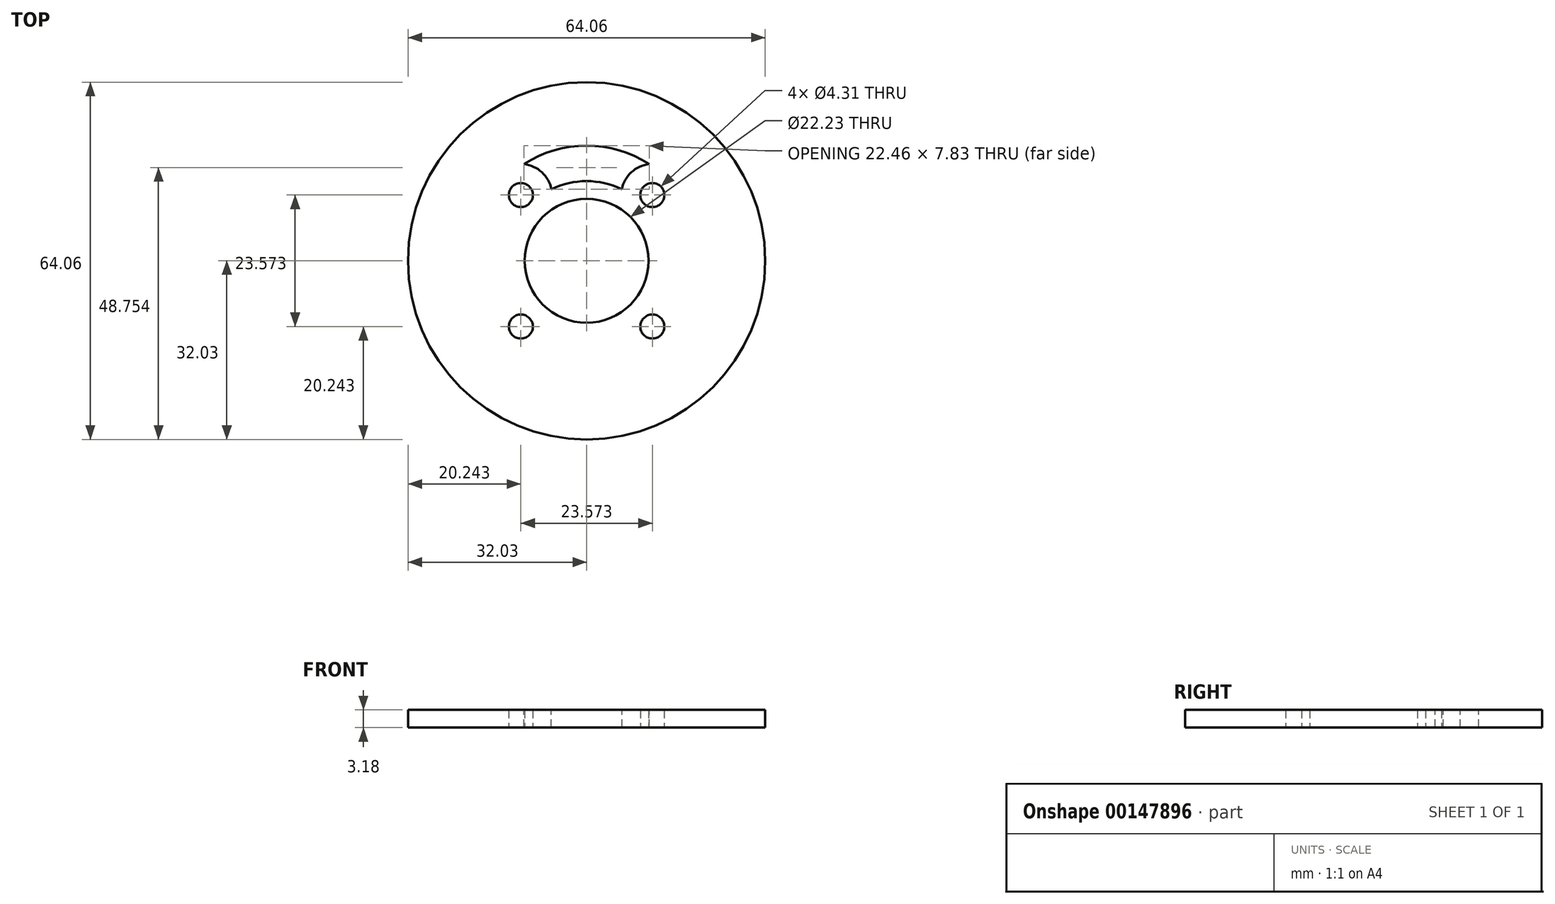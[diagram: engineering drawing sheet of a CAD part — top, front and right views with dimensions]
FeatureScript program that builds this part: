
annotation { "Feature Type Name" : "Feature", "Feature Type Description" : "" }
export const myFeature = defineFeature(function(context is Context, id is Id, definition is map)
    precondition{}
    {
        {
            var Q0;
            Q0=qCreatedBy(makeId("Top.planeOp"),FACE);
            var sketch = newSketch(context, id + "F0", { "sketchPlane" : qUnion([Q0])});
            skCircle(sketch, "E0", {"center": v(0, 0) * mm, "radius": 32.03 * mm});
            skCircle(sketch, "E1", {"center": v(0, 0) * mm, "radius": 11.11 * mm, "construction": true});
            skLineSegment(sketch, "E2.bottom", {"start": v(-11.79, -11.79) * mm, "end": v(11.79, -11.79) * mm, "construction": true});
            skLineSegment(sketch, "E2.top", {"start": v(-11.79, 11.79) * mm, "end": v(11.79, 11.79) * mm, "construction": true});
            skLineSegment(sketch, "E2.left", {"start": v(-11.79, -11.79) * mm, "end": v(-11.79, 11.79) * mm, "construction": true});
            skLineSegment(sketch, "E2.right", {"start": v(11.79, -11.79) * mm, "end": v(11.79, 11.79) * mm, "construction": true});
            skCircle(sketch, "E3", {"center": v(-11.79, -11.79) * mm, "radius": 5.56 * mm, "construction": true});
            skCircle(sketch, "E4", {"center": v(-11.79, -11.79) * mm, "radius": 2.15 * mm});
            skCircle(sketch, "E5", {"center": v(11.79, 11.79) * mm, "radius": 2.15 * mm});
            skCircle(sketch, "E6", {"center": v(11.79, -11.79) * mm, "radius": 2.15 * mm});
            skCircle(sketch, "E7", {"center": v(-11.79, 11.79) * mm, "radius": 2.15 * mm});
            skCircle(sketch, "E8", {"center": v(0, 0) * mm, "radius": 11.11 * mm});
            skSolve(sketch);
        }
        {
            var Q0;
            Q0=makeQuery(id+"F0.imprint","IMPRINT",FACE,{"disambiguationData":[TD([[makeQuery(id+"F0.imprint","IMPRINT",EDGE,{"derivedFrom":sQuery(id+"F0.wireOp",EDGE,"d7zeTPih-CRss-xDOh-gPdP-rmPCdwzH7cdN.left")}),1.0]])]});
            var Q1;
            Q1=makeQuery(id+"F0.imprint","IMPRINT",FACE,{"disambiguationData":[TD([[makeQuery(id+"F0.imprint","IMPRINT",EDGE,{"derivedFrom":sQuery(id+"F0.wireOp",EDGE,"E0")}),1.0]])]});
            extrude(context, id + "F1", {"entities" : qUnion([Q0, Q1]), "depth" : 3.17 * mm});
        }
        {
            var Q0;
            Q0=makeQuery(id+"F1.opExtrude","CAP_FACE",FACE,{"disambiguationData":[OSD([sQuery(id+"F0.wireOp",EDGE,"E0"),sQuery(id+"F0.wireOp",EDGE,"E4"),sQuery(id+"F0.wireOp",EDGE,"E5"),sQuery(id+"F0.wireOp",EDGE,"E6"),sQuery(id+"F0.wireOp",EDGE,"E7"),sQuery(id+"F0.wireOp",EDGE,"E8")])],"isStart":false});
            var sketch = newSketch(context, id + "F2", { "sketchPlane" : qUnion([Q0])});
            skArc(sketch, "E9", {"start": v(-6.33, 12.81) * mm, "mid": v(-8.03, 15.88) * mm, "end": v(-11.23, 17.31) * mm});
            skArc(sketch, "E10", {"start": v(11.23, 17.31) * mm, "mid": v(8.03, 15.88) * mm, "end": v(6.33, 12.81) * mm});
            skArc(sketch, "E11", {"start": v(11.23, 17.31) * mm, "mid": v(0, 20.64) * mm, "end": v(-11.23, 17.31) * mm});
            skArc(sketch, "E12", {"start": v(6.33, 12.81) * mm, "mid": v(0, 14.29) * mm, "end": v(-6.33, 12.81) * mm});
            skSolve(sketch);
        }
        {
            var Q0;
            Q0=qSketchRegion(id+"F2",true);
            var Q1;
            Q1=makeQuery(id+"F1.opExtrude","CAP_FACE",FACE,{"disambiguationData":[OSD([sQuery(id+"F0.wireOp",EDGE,"E0"),sQuery(id+"F0.wireOp",EDGE,"E4"),sQuery(id+"F0.wireOp",EDGE,"E5"),sQuery(id+"F0.wireOp",EDGE,"E6"),sQuery(id+"F0.wireOp",EDGE,"E7"),sQuery(id+"F0.wireOp",EDGE,"E8")])],"isStart":true});
            extrude(context, id + "F3", {"entities" : qUnion([Q0]), "operationType" : NewBodyOperationType.REMOVE, "endBound" : BoundingType.UP_TO_SURFACE, "oppositeDirection" : true, "endBoundEntityFace" : qUnion([Q1]), "depth" : 25.4 * mm});
        }
    });
